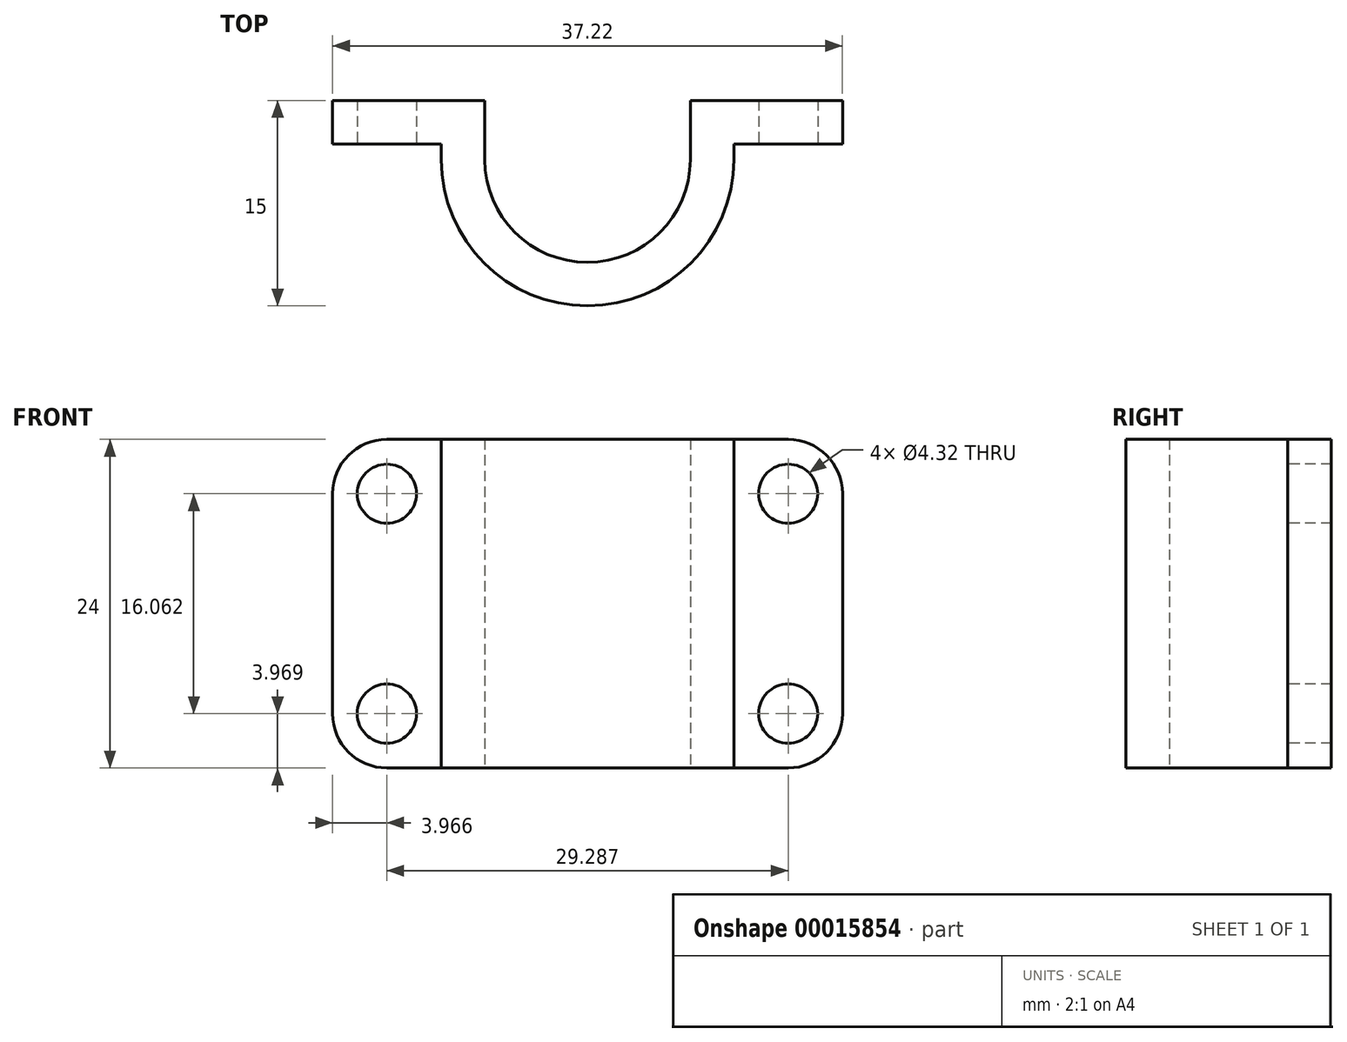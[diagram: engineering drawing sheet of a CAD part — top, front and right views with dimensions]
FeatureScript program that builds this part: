
annotation { "Feature Type Name" : "Feature", "Feature Type Description" : "" }
export const myFeature = defineFeature(function(context is Context, id is Id, definition is map)
    precondition{}
    {
        {
            var Q0;
            Q0=qCreatedBy(makeId("Top.planeOp"),FACE);
            var sketch = newSketch(context, id + "F0", { "sketchPlane" : qUnion([Q0])});
            skLineSegment(sketch, "E0.bottom", {"start": v(0, 0) * mm, "end": v(15, 0) * mm, "construction": true});
            skLineSegment(sketch, "E0.top", {"start": v(0, -4.32) * mm, "end": v(15, -4.32) * mm, "construction": true});
            skLineSegment(sketch, "E0.left", {"start": v(0, 0) * mm, "end": v(0, -4.32) * mm});
            skLineSegment(sketch, "E0.right", {"start": v(15, 0) * mm, "end": v(15, -4.32) * mm});
            skArc(sketch, "E1", {"start": v(0, -4.32) * mm, "mid": v(7.5, -11.82) * mm, "end": v(15, -4.32) * mm});
            skLineSegment(sketch, "E2", {"start": v(0, 0) * mm, "end": v(-11.11, 0) * mm});
            skLineSegment(sketch, "E3", {"start": v(-11.11, 0) * mm, "end": v(-11.11, -3.18) * mm});
            skLineSegment(sketch, "E4.bottom", {"start": v(-11.11, -3.18) * mm, "end": v(-3.17, -3.18) * mm});
            skLineSegment(sketch, "E4.right", {"start": v(-3.17, -3.18) * mm, "end": v(-3.17, -4.32) * mm});
            skLineSegment(sketch, "E5.bottom", {"start": v(15, 0) * mm, "end": v(26.11, 0) * mm});
            skLineSegment(sketch, "E5.top", {"start": v(18.17, -3.18) * mm, "end": v(26.11, -3.18) * mm});
            skLineSegment(sketch, "E5.right", {"start": v(26.11, 0) * mm, "end": v(26.11, -3.18) * mm});
            skLineSegment(sketch, "E6.right", {"start": v(18.17, -3.18) * mm, "end": v(18.17, -4.32) * mm});
            skLineSegment(sketch, "E7", {"start": v(0, -4.32) * mm, "end": v(-3.17, -4.32) * mm, "construction": true});
            skLineSegment(sketch, "E8", {"start": v(15, -4.32) * mm, "end": v(18.17, -4.32) * mm, "construction": true});
            skArc(sketch, "E9", {"start": v(-3.17, -4.32) * mm, "mid": v(7.5, -15) * mm, "end": v(18.17, -4.32) * mm});
            skSolve(sketch);
        }
        {
            var Q0;
            Q0 = qSketchRegion(id + "F0", true);
            extrude(context, id + "F1", {"entities" : qUnion([Q0]), "depth" : 24 * mm});
        }
        {
            var Q0;
            Q0=makeQuery(id+"F1.opExtrude","SWEPT_FACE",FACE,{"disambiguationData":[OSD([sQuery(id+"F0.wireOp",EDGE,"E4.bottom")])]});
            var sketch = newSketch(context, id + "F2", { "sketchPlane" : qUnion([Q0])});
            skCircle(sketch, "E10", {"center": v(-7.14, 20.03) * mm, "radius": 2.16 * mm});
            skLineSegment(sketch, "E11", {"start": v(-7.14, 24) * mm, "end": v(-7.14, 20.03) * mm});
            skLineSegment(sketch, "E12", {"start": v(22.14, 24) * mm, "end": v(22.14, 20.03) * mm});
            skLineSegment(sketch, "E13", {"start": v(22.14, 0) * mm, "end": v(22.14, 3.97) * mm});
            skLineSegment(sketch, "E14", {"start": v(-7.14, 0) * mm, "end": v(-7.14, 3.97) * mm});
            skCircle(sketch, "E15", {"center": v(22.14, 20.03) * mm, "radius": 2.16 * mm});
            skCircle(sketch, "E16", {"center": v(22.14, 3.97) * mm, "radius": 2.16 * mm});
            skCircle(sketch, "E17", {"center": v(-7.14, 3.97) * mm, "radius": 2.16 * mm});
            skSolve(sketch);
        }
        {
            var Q0;
            Q0 = qSketchRegion(id + "F2", true);
            extrude(context, id + "F3", {"entities" : qUnion([Q0]), "operationType" : NewBodyOperationType.REMOVE, "oppositeDirection" : true, "depth" : 25.4 * mm});
        }
        {
            var Q0;
            Q0=makeQuery(id+"F1.opExtrude","CAP_EDGE",EDGE,{"disambiguationData":[OSD([sQuery(id+"F0.wireOp",EDGE,"E3")])],"isStart":false});
            var Q1;
            Q1=makeQuery(id+"F1.opExtrude","CAP_EDGE",EDGE,{"disambiguationData":[OSD([sQuery(id+"F0.wireOp",EDGE,"E3")])],"isStart":true});
            var Q2;
            Q2=makeQuery(id+"F1.opExtrude","CAP_EDGE",EDGE,{"disambiguationData":[OSD([sQuery(id+"F0.wireOp",EDGE,"E5.right")])],"isStart":false});
            var Q3;
            Q3=makeQuery(id+"F1.opExtrude","CAP_EDGE",EDGE,{"disambiguationData":[OSD([sQuery(id+"F0.wireOp",EDGE,"E5.right")])],"isStart":true});
            fillet(context, id + "F4", {"entities" : qUnion([Q0, Q1, Q2, Q3]), "radius" : 3.97 * mm, "tangentPropagation" : true, "allowEdgeOverflow" : false});
        }
    });
